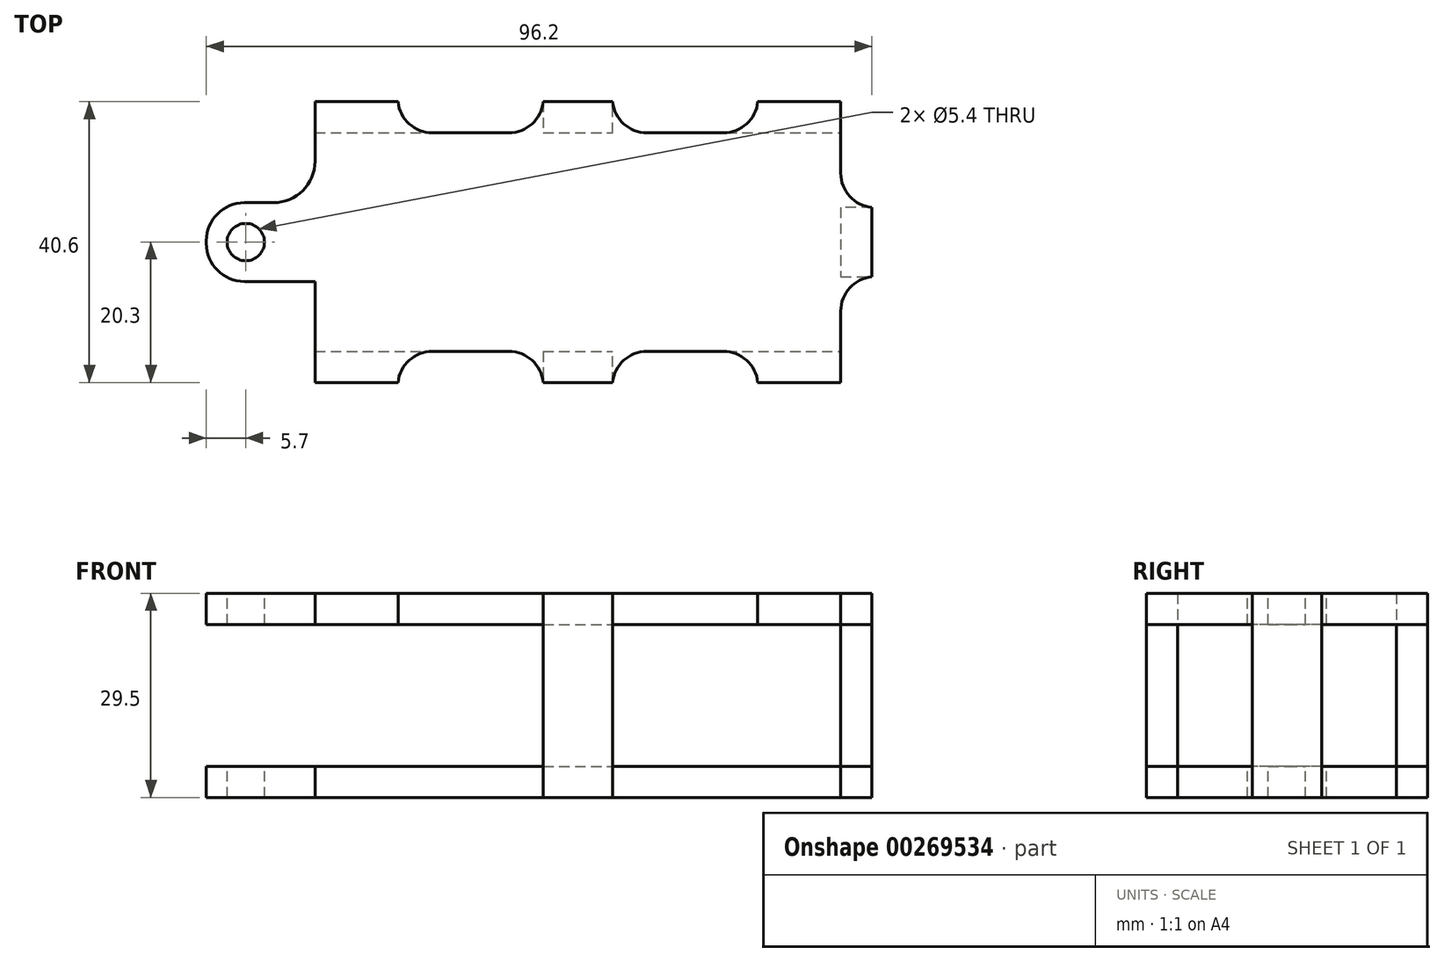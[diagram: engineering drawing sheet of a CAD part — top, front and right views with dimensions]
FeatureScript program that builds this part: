
annotation { "Feature Type Name" : "Feature", "Feature Type Description" : "" }
export const myFeature = defineFeature(function(context is Context, id is Id, definition is map)
    precondition{}
    {
        {
            var Q0;
            Q0=qCreatedBy(makeId("Top.planeOp"),FACE);
            var sketch = newSketch(context, id + "F0", { "sketchPlane" : qUnion([Q0])});
            skLineSegment(sketch, "E0.bottom", {"start": v(0, 31.6) * mm, "end": v(76, 31.6) * mm});
            skLineSegment(sketch, "E0.top", {"start": v(0, 0) * mm, "end": v(76, 0) * mm});
            skLineSegment(sketch, "E0.left", {"start": v(0, 31.6) * mm, "end": v(0, 0) * mm});
            skLineSegment(sketch, "E0.right", {"start": v(76, 31.6) * mm, "end": v(76, 0) * mm});
            skLineSegment(sketch, "E1.bottom", {"start": v(76, 31.6) * mm, "end": v(64, 31.6) * mm});
            skLineSegment(sketch, "E1.top", {"start": v(76, 36.1) * mm, "end": v(64, 36.1) * mm});
            skLineSegment(sketch, "E1.left", {"start": v(76, 31.6) * mm, "end": v(76, 36.1) * mm});
            skLineSegment(sketch, "E1.right", {"start": v(64, 31.6) * mm, "end": v(64, 36.1) * mm});
            skLineSegment(sketch, "E2.bottom", {"start": v(76, 0) * mm, "end": v(64, 0) * mm});
            skLineSegment(sketch, "E2.top", {"start": v(76, -4.5) * mm, "end": v(64, -4.5) * mm});
            skLineSegment(sketch, "E2.left", {"start": v(76, 0) * mm, "end": v(76, -4.5) * mm});
            skLineSegment(sketch, "E2.right", {"start": v(64, 0) * mm, "end": v(64, -4.5) * mm});
            skLineSegment(sketch, "E3.bottom", {"start": v(76, 10.8) * mm, "end": v(80.5, 10.8) * mm});
            skLineSegment(sketch, "E3.top", {"start": v(76, 20.8) * mm, "end": v(80.5, 20.8) * mm});
            skLineSegment(sketch, "E3.left", {"start": v(76, 10.8) * mm, "end": v(76, 20.8) * mm});
            skLineSegment(sketch, "E3.right", {"start": v(80.5, 10.8) * mm, "end": v(80.5, 20.8) * mm});
            skPoint(sketch, "E4", {"position": v(80.5, 15.8) * mm});
            skPoint(sketch, "E5", {"position": v(76, 15.8) * mm});
            skLineSegment(sketch, "E6", {"start": v(80.5, 15.8) * mm, "end": v(76, 15.8) * mm});
            skLineSegment(sketch, "E7.bottom", {"start": v(0, 0) * mm, "end": v(12, 0) * mm});
            skLineSegment(sketch, "E7.top", {"start": v(0, -4.5) * mm, "end": v(12, -4.5) * mm});
            skLineSegment(sketch, "E7.left", {"start": v(0, 0) * mm, "end": v(0, -4.5) * mm});
            skLineSegment(sketch, "E7.right", {"start": v(12, 0) * mm, "end": v(12, -4.5) * mm});
            skLineSegment(sketch, "E8.bottom", {"start": v(0, 31.6) * mm, "end": v(12, 31.6) * mm});
            skLineSegment(sketch, "E8.top", {"start": v(0, 36.1) * mm, "end": v(12, 36.1) * mm});
            skLineSegment(sketch, "E8.left", {"start": v(0, 31.6) * mm, "end": v(0, 36.1) * mm});
            skLineSegment(sketch, "E8.right", {"start": v(12, 31.6) * mm, "end": v(12, 36.1) * mm});
            skPoint(sketch, "E9", {"position": v(38, 0) * mm});
            skPoint(sketch, "E10", {"position": v(38, 31.6) * mm});
            skLineSegment(sketch, "E11.bottom", {"start": v(43, 31.6) * mm, "end": v(33, 31.6) * mm});
            skLineSegment(sketch, "E11.top", {"start": v(43, 36.1) * mm, "end": v(33, 36.1) * mm});
            skLineSegment(sketch, "E11.left", {"start": v(43, 31.6) * mm, "end": v(43, 36.1) * mm});
            skLineSegment(sketch, "E11.right", {"start": v(33, 31.6) * mm, "end": v(33, 36.1) * mm});
            skPoint(sketch, "E11.middle", {"position": v(38, 33.85) * mm});
            skLineSegment(sketch, "E12.bottom", {"start": v(43, 0) * mm, "end": v(33, 0) * mm});
            skLineSegment(sketch, "E12.top", {"start": v(43, -4.5) * mm, "end": v(33, -4.5) * mm});
            skLineSegment(sketch, "E12.left", {"start": v(43, 0) * mm, "end": v(43, -4.5) * mm});
            skLineSegment(sketch, "E12.right", {"start": v(33, 0) * mm, "end": v(33, -4.5) * mm});
            skPoint(sketch, "E12.middle", {"position": v(38, -2.25) * mm});
            skLineSegment(sketch, "E13", {"start": v(38, 33.85) * mm, "end": v(38, 31.6) * mm});
            skLineSegment(sketch, "E14", {"start": v(38, 0) * mm, "end": v(38, -2.25) * mm});
            skSolve(sketch);
        }
        {
            var Q0;
            Q0=makeQuery(id+"F0.imprint","IMPRINT",FACE,{"disambiguationData":[TD([[makeQuery(id+"F0.imprint","IMPRINT",EDGE,{"derivedFrom":sQuery(id+"F0.wireOp",EDGE,"E0.left")}),1.0]])]});
            var Q1;
            Q1=makeQuery(id+"F0.imprint","IMPRINT",FACE,{"disambiguationData":[TD([[makeQuery(id+"F0.imprint","IMPRINT",EDGE,{"derivedFrom":sQuery(id+"F0.wireOp",EDGE,"E7.bottom")}),-1.0]])]});
            var Q2;
            Q2=makeQuery(id+"F0.imprint","IMPRINT",FACE,{"disambiguationData":[TD([[makeQuery(id+"F0.imprint","IMPRINT",EDGE,{"derivedFrom":sQuery(id+"F0.wireOp",EDGE,"E12.top")}),-1.0]])]});
            var Q3;
            Q3=makeQuery(id+"F0.imprint","IMPRINT",FACE,{"disambiguationData":[TD([[makeQuery(id+"F0.imprint","IMPRINT",EDGE,{"derivedFrom":sQuery(id+"F0.wireOp",EDGE,"E2.bottom")}),1.0]])]});
            var Q4;
            {var subQ0=sQuery(id+"F0.wireOp",EDGE,"E3.bottom");Q4=makeQuery(id+"F0.imprint","IMPRINT",FACE,{"disambiguationData":[TD([[makeQuery(id+"F0.imprint","IMPRINT",EDGE,{"derivedFrom":subQ0}),1.0]])]});}
            var Q5;
            {var subQ0=sQuery(id+"F0.wireOp",EDGE,"E3.top");Q5=makeQuery(id+"F0.imprint","IMPRINT",FACE,{"disambiguationData":[TD([[makeQuery(id+"F0.imprint","IMPRINT",EDGE,{"derivedFrom":subQ0}),-1.0]])]});}
            var Q6;
            Q6=makeQuery(id+"F0.imprint","IMPRINT",FACE,{"disambiguationData":[TD([[makeQuery(id+"F0.imprint","IMPRINT",EDGE,{"derivedFrom":sQuery(id+"F0.wireOp",EDGE,"E1.bottom")}),-1.0]])]});
            var Q7;
            Q7=makeQuery(id+"F0.imprint","IMPRINT",FACE,{"disambiguationData":[TD([[makeQuery(id+"F0.imprint","IMPRINT",EDGE,{"derivedFrom":sQuery(id+"F0.wireOp",EDGE,"E11.top")}),1.0]])]});
            var Q8;
            Q8=makeQuery(id+"F0.imprint","IMPRINT",FACE,{"disambiguationData":[TD([[makeQuery(id+"F0.imprint","IMPRINT",EDGE,{"derivedFrom":sQuery(id+"F0.wireOp",EDGE,"E8.bottom")}),1.0]])]});
            extrude(context, id + "F1", {"entities" : qUnion([Q0, Q1, Q2, Q3, Q4, Q5, Q6, Q7, Q8]), "oppositeDirection" : true, "depth" : 4.5 * mm});
        }
        {
            var Q0;
            Q0=makeQuery(id+"F0.imprint","IMPRINT",FACE,{"disambiguationData":[TD([[makeQuery(id+"F0.imprint","IMPRINT",EDGE,{"derivedFrom":sQuery(id+"F0.wireOp",EDGE,"E7.bottom")}),-1.0]])]});
            var Q1;
            Q1=makeQuery(id+"F0.imprint","IMPRINT",FACE,{"disambiguationData":[TD([[makeQuery(id+"F0.imprint","IMPRINT",EDGE,{"derivedFrom":sQuery(id+"F0.wireOp",EDGE,"E12.top")}),-1.0]])]});
            var Q2;
            Q2=makeQuery(id+"F0.imprint","IMPRINT",FACE,{"disambiguationData":[TD([[makeQuery(id+"F0.imprint","IMPRINT",EDGE,{"derivedFrom":sQuery(id+"F0.wireOp",EDGE,"E11.top")}),1.0]])]});
            var Q3;
            Q3=makeQuery(id+"F0.imprint","IMPRINT",FACE,{"disambiguationData":[TD([[makeQuery(id+"F0.imprint","IMPRINT",EDGE,{"derivedFrom":sQuery(id+"F0.wireOp",EDGE,"E8.bottom")}),1.0]])]});
            var Q4;
            Q4=makeQuery(id+"F0.imprint","IMPRINT",FACE,{"disambiguationData":[TD([[makeQuery(id+"F0.imprint","IMPRINT",EDGE,{"derivedFrom":sQuery(id+"F0.wireOp",EDGE,"E2.bottom")}),1.0]])]});
            var Q5;
            {var subQ0=sQuery(id+"F0.wireOp",EDGE,"E3.bottom");Q5=makeQuery(id+"F0.imprint","IMPRINT",FACE,{"disambiguationData":[TD([[makeQuery(id+"F0.imprint","IMPRINT",EDGE,{"derivedFrom":subQ0}),1.0]])]});}
            var Q6;
            {var subQ0=sQuery(id+"F0.wireOp",EDGE,"E3.top");Q6=makeQuery(id+"F0.imprint","IMPRINT",FACE,{"disambiguationData":[TD([[makeQuery(id+"F0.imprint","IMPRINT",EDGE,{"derivedFrom":subQ0}),-1.0]])]});}
            var Q7;
            Q7=makeQuery(id+"F0.imprint","IMPRINT",FACE,{"disambiguationData":[TD([[makeQuery(id+"F0.imprint","IMPRINT",EDGE,{"derivedFrom":sQuery(id+"F0.wireOp",EDGE,"E1.bottom")}),-1.0]])]});
            extrude(context, id + "F2", {"entities" : qUnion([Q0, Q1, Q2, Q3, Q4, Q5, Q6, Q7]), "operationType" : NewBodyOperationType.ADD, "depth" : 20.5 * mm});
        }
        {
            var Q0;
            Q0 = qSketchRegion(id + "F0", true);
            extrude(context, id + "F3", {"entities" : qUnion([Q0]), "operationType" : NewBodyOperationType.ADD, "depth" : 25 * mm, "hasSecondDirection" : true, "secondDirectionOppositeDirection" : false, "secondDirectionDepth" : 20.5 * mm});
        }
        {
            var Q0;
            Q0=makeQuery(id+"F3.opExtrude","SWEPT_EDGE",EDGE,{"disambiguationData":[OSD([sQuery(id+"F0.wireOp",EDGE,"E0.top"),sQuery(id+"F0.wireOp",EDGE,"E7.bottom"),sQuery(id+"F0.wireOp",EDGE,"E7.right")])]});
            var Q1;
            Q1=makeQuery(id+"F1.opExtrude","SWEPT_EDGE",EDGE,{"disambiguationData":[OSD([sQuery(id+"F0.wireOp",EDGE,"E0.top"),sQuery(id+"F0.wireOp",EDGE,"E7.bottom"),sQuery(id+"F0.wireOp",EDGE,"E7.right")])]});
            var Q2;
            Q2=makeQuery(id+"F3.opExtrude","SWEPT_EDGE",EDGE,{"disambiguationData":[OSD([sQuery(id+"F0.wireOp",EDGE,"E0.top"),sQuery(id+"F0.wireOp",EDGE,"E12.bottom"),sQuery(id+"F0.wireOp",EDGE,"E12.right")])]});
            var Q3;
            Q3=makeQuery(id+"F1.opExtrude","SWEPT_EDGE",EDGE,{"disambiguationData":[OSD([sQuery(id+"F0.wireOp",EDGE,"E0.top"),sQuery(id+"F0.wireOp",EDGE,"E12.bottom"),sQuery(id+"F0.wireOp",EDGE,"E12.right")])]});
            var Q4;
            Q4=makeQuery(id+"F3.opExtrude","SWEPT_EDGE",EDGE,{"disambiguationData":[OSD([sQuery(id+"F0.wireOp",EDGE,"E0.top"),sQuery(id+"F0.wireOp",EDGE,"E12.bottom"),sQuery(id+"F0.wireOp",EDGE,"E12.left")])]});
            var Q5;
            Q5=makeQuery(id+"F1.opExtrude","SWEPT_EDGE",EDGE,{"disambiguationData":[OSD([sQuery(id+"F0.wireOp",EDGE,"E0.top"),sQuery(id+"F0.wireOp",EDGE,"E12.bottom"),sQuery(id+"F0.wireOp",EDGE,"E12.left")])]});
            var Q6;
            Q6=makeQuery(id+"F1.opExtrude","SWEPT_EDGE",EDGE,{"disambiguationData":[OSD([sQuery(id+"F0.wireOp",EDGE,"E0.top"),sQuery(id+"F0.wireOp",EDGE,"E2.bottom"),sQuery(id+"F0.wireOp",EDGE,"E2.right")])]});
            var Q7;
            Q7=makeQuery(id+"F3.opExtrude","SWEPT_EDGE",EDGE,{"disambiguationData":[OSD([sQuery(id+"F0.wireOp",EDGE,"E0.top"),sQuery(id+"F0.wireOp",EDGE,"E2.bottom"),sQuery(id+"F0.wireOp",EDGE,"E2.right")])]});
            var Q8;
            Q8=makeQuery(id+"F3.opExtrude","SWEPT_EDGE",EDGE,{"disambiguationData":[OSD([sQuery(id+"F0.wireOp",EDGE,"E0.right"),sQuery(id+"F0.wireOp",EDGE,"E3.bottom"),sQuery(id+"F0.wireOp",EDGE,"E3.left")])]});
            var Q9;
            Q9=makeQuery(id+"F1.opExtrude","SWEPT_EDGE",EDGE,{"disambiguationData":[OSD([sQuery(id+"F0.wireOp",EDGE,"E0.right"),sQuery(id+"F0.wireOp",EDGE,"E3.bottom"),sQuery(id+"F0.wireOp",EDGE,"E3.left")])]});
            var Q10;
            Q10=makeQuery(id+"F3.opExtrude","SWEPT_EDGE",EDGE,{"disambiguationData":[OSD([sQuery(id+"F0.wireOp",EDGE,"E0.right"),sQuery(id+"F0.wireOp",EDGE,"E3.top"),sQuery(id+"F0.wireOp",EDGE,"E3.left")])]});
            var Q11;
            Q11=makeQuery(id+"F1.opExtrude","SWEPT_EDGE",EDGE,{"disambiguationData":[OSD([sQuery(id+"F0.wireOp",EDGE,"E0.right"),sQuery(id+"F0.wireOp",EDGE,"E3.top"),sQuery(id+"F0.wireOp",EDGE,"E3.left")])]});
            var Q12;
            Q12=makeQuery(id+"F3.opExtrude","SWEPT_EDGE",EDGE,{"disambiguationData":[OSD([sQuery(id+"F0.wireOp",EDGE,"E0.bottom"),sQuery(id+"F0.wireOp",EDGE,"E11.bottom"),sQuery(id+"F0.wireOp",EDGE,"E11.left")])]});
            var Q13;
            Q13=makeQuery(id+"F1.opExtrude","SWEPT_EDGE",EDGE,{"disambiguationData":[OSD([sQuery(id+"F0.wireOp",EDGE,"E0.bottom"),sQuery(id+"F0.wireOp",EDGE,"E11.bottom"),sQuery(id+"F0.wireOp",EDGE,"E11.left")])]});
            var Q14;
            Q14=makeQuery(id+"F3.opExtrude","SWEPT_EDGE",EDGE,{"disambiguationData":[OSD([sQuery(id+"F0.wireOp",EDGE,"E0.bottom"),sQuery(id+"F0.wireOp",EDGE,"E8.bottom"),sQuery(id+"F0.wireOp",EDGE,"E8.right")])]});
            var Q15;
            Q15=makeQuery(id+"F1.opExtrude","SWEPT_EDGE",EDGE,{"disambiguationData":[OSD([sQuery(id+"F0.wireOp",EDGE,"E0.bottom"),sQuery(id+"F0.wireOp",EDGE,"E8.bottom"),sQuery(id+"F0.wireOp",EDGE,"E8.right")])]});
            var Q16;
            Q16=makeQuery(id+"F3.opExtrude","SWEPT_EDGE",EDGE,{"disambiguationData":[OSD([sQuery(id+"F0.wireOp",EDGE,"E0.bottom"),sQuery(id+"F0.wireOp",EDGE,"E1.bottom"),sQuery(id+"F0.wireOp",EDGE,"E1.right")])]});
            var Q17;
            Q17=makeQuery(id+"F1.opExtrude","SWEPT_EDGE",EDGE,{"disambiguationData":[OSD([sQuery(id+"F0.wireOp",EDGE,"E0.bottom"),sQuery(id+"F0.wireOp",EDGE,"E1.bottom"),sQuery(id+"F0.wireOp",EDGE,"E1.right")])]});
            fillet(context, id + "F4", {"entities" : qUnion([Q0, Q1, Q2, Q3, Q4, Q5, Q6, Q7, Q8, Q9, Q10, Q11, Q12, Q13, Q14, Q15, Q16, Q17]), "radius" : 5 * mm, "tangentPropagation" : true, "allowEdgeOverflow" : false});
        }
        {
            var Q0;
            Q0=makeQuery(id+"F3.opExtrude","SWEPT_EDGE",EDGE,{"disambiguationData":[OSD([sQuery(id+"F0.wireOp",EDGE,"E0.bottom"),sQuery(id+"F0.wireOp",EDGE,"E11.bottom"),sQuery(id+"F0.wireOp",EDGE,"E11.right")])]});
            var Q1;
            Q1=makeQuery(id+"F1.opExtrude","SWEPT_EDGE",EDGE,{"disambiguationData":[OSD([sQuery(id+"F0.wireOp",EDGE,"E0.bottom"),sQuery(id+"F0.wireOp",EDGE,"E11.bottom"),sQuery(id+"F0.wireOp",EDGE,"E11.right")])]});
            fillet(context, id + "F5", {"entities" : qUnion([Q0, Q1]), "radius" : 5 * mm, "tangentPropagation" : true, "allowEdgeOverflow" : false});
        }
        {
            var Q0;
            Q0=makeQuery(id+"F3.opExtrude","CAP_FACE",FACE,{"disambiguationData":[OSD([sQuery(id+"F0.wireOp",EDGE,"E0.bottom"),sQuery(id+"F0.wireOp",EDGE,"E0.top"),sQuery(id+"F0.wireOp",EDGE,"E0.left"),sQuery(id+"F0.wireOp",EDGE,"E0.right"),sQuery(id+"F0.wireOp",EDGE,"E1.top"),sQuery(id+"F0.wireOp",EDGE,"E1.left"),sQuery(id+"F0.wireOp",EDGE,"E1.right"),sQuery(id+"F0.wireOp",EDGE,"E2.top"),sQuery(id+"F0.wireOp",EDGE,"E2.left"),sQuery(id+"F0.wireOp",EDGE,"E2.right"),sQuery(id+"F0.wireOp",EDGE,"E3.bottom"),sQuery(id+"F0.wireOp",EDGE,"E3.top"),sQuery(id+"F0.wireOp",EDGE,"E3.right"),sQuery(id+"F0.wireOp",EDGE,"E7.top"),sQuery(id+"F0.wireOp",EDGE,"E7.left"),sQuery(id+"F0.wireOp",EDGE,"E7.right"),sQuery(id+"F0.wireOp",EDGE,"E8.top"),sQuery(id+"F0.wireOp",EDGE,"E8.left"),sQuery(id+"F0.wireOp",EDGE,"E8.right"),sQuery(id+"F0.wireOp",EDGE,"E11.top"),sQuery(id+"F0.wireOp",EDGE,"E11.left"),sQuery(id+"F0.wireOp",EDGE,"E11.right"),sQuery(id+"F0.wireOp",EDGE,"E12.top"),sQuery(id+"F0.wireOp",EDGE,"E12.left"),sQuery(id+"F0.wireOp",EDGE,"E12.right")])],"isStart":false});
            var sketch = newSketch(context, id + "F6", { "sketchPlane" : qUnion([Q0])});
            skPoint(sketch, "E15", {"position": v(0, 15.8) * mm});
            skCircle(sketch, "E16", {"center": v(-10, 15.8) * mm, "radius": 2.7 * mm});
            skLineSegment(sketch, "E17.bottom", {"start": v(0, 21.5) * mm, "end": v(-15.7, 21.5) * mm});
            skLineSegment(sketch, "E17.top", {"start": v(0, 10.1) * mm, "end": v(-15.7, 10.1) * mm});
            skLineSegment(sketch, "E17.left", {"start": v(0, 21.5) * mm, "end": v(0, 10.1) * mm});
            skLineSegment(sketch, "E17.right", {"start": v(-15.7, 21.5) * mm, "end": v(-15.7, 10.1) * mm});
            skSolve(sketch);
        }
        {
            var Q0;
            Q0=makeQuery(id+"F6.imprint","IMPRINT",FACE,{"disambiguationData":[TD([[makeQuery(id+"F6.imprint","IMPRINT",EDGE,{"derivedFrom":sQuery(id+"F6.wireOp",EDGE,"E16")}),-1.0]])]});
            extrude(context, id + "F7", {"entities" : qUnion([Q0]), "operationType" : NewBodyOperationType.ADD, "oppositeDirection" : true, "depth" : 29.5 * mm, "hasSecondDirection" : true, "secondDirectionOppositeDirection" : true, "secondDirectionDepth" : 25 * mm});
        }
        {
            var Q0;
            Q0=makeQuery(id+"F6.imprint","IMPRINT",FACE,{"disambiguationData":[TD([[makeQuery(id+"F6.imprint","IMPRINT",EDGE,{"derivedFrom":sQuery(id+"F6.wireOp",EDGE,"E16")}),-1.0]])]});
            extrude(context, id + "F8", {"entities" : qUnion([Q0]), "operationType" : NewBodyOperationType.ADD, "oppositeDirection" : true, "depth" : 4.5 * mm});
        }
        {
            var Q0;
            Q0=makeQuery(id+"F8.opExtrude","SWEPT_EDGE",EDGE,{"disambiguationData":[OSD([sQuery(id+"F0.wireOp",EDGE,"E0.left"),sQuery(id+"F0.wireOp",EDGE,"E7.left"),sQuery(id+"F0.wireOp",EDGE,"E8.left"),sQuery(id+"F6.wireOp",EDGE,"E17.bottom"),sQuery(id+"F6.wireOp",EDGE,"E17.left")])]});
            var Q1;
            Q1=makeQuery(id+"F8.opExtrude","SWEPT_EDGE",EDGE,{"disambiguationData":[OSD([sQuery(id+"F0.wireOp",EDGE,"E0.left"),sQuery(id+"F0.wireOp",EDGE,"E7.left"),sQuery(id+"F0.wireOp",EDGE,"E8.left"),sQuery(id+"F6.wireOp",EDGE,"E17.top"),sQuery(id+"F6.wireOp",EDGE,"E17.left")])]});
            var Q2;
            Q2=makeQuery(id+"F7.opExtrude","SWEPT_EDGE",EDGE,{"disambiguationData":[OSD([sQuery(id+"F0.wireOp",EDGE,"E0.left"),sQuery(id+"F0.wireOp",EDGE,"E7.left"),sQuery(id+"F0.wireOp",EDGE,"E8.left"),sQuery(id+"F6.wireOp",EDGE,"E17.top"),sQuery(id+"F6.wireOp",EDGE,"E17.left")])]});
            var Q3;
            Q3=makeQuery(id+"F7.opExtrude","SWEPT_EDGE",EDGE,{"disambiguationData":[OSD([sQuery(id+"F0.wireOp",EDGE,"E0.left"),sQuery(id+"F0.wireOp",EDGE,"E7.left"),sQuery(id+"F0.wireOp",EDGE,"E8.left"),sQuery(id+"F6.wireOp",EDGE,"E17.bottom"),sQuery(id+"F6.wireOp",EDGE,"E17.left")])]});
            fillet(context, id + "F9", {"entities" : qUnion([Q0, Q1, Q2, Q3]), "radius" : 6 * mm, "tangentPropagation" : true, "allowEdgeOverflow" : false});
        }
        {
            var Q0;
            Q0=makeQuery(id+"F8.opExtrude","SWEPT_EDGE",EDGE,{"disambiguationData":[OSD([sQuery(id+"F6.wireOp",EDGE,"E17.bottom"),sQuery(id+"F6.wireOp",EDGE,"E17.right")])]});
            var Q1;
            Q1=makeQuery(id+"F8.opExtrude","SWEPT_EDGE",EDGE,{"disambiguationData":[OSD([sQuery(id+"F6.wireOp",EDGE,"E17.top"),sQuery(id+"F6.wireOp",EDGE,"E17.right")])]});
            var Q2;
            Q2=makeQuery(id+"F7.opExtrude","SWEPT_EDGE",EDGE,{"disambiguationData":[OSD([sQuery(id+"F6.wireOp",EDGE,"E17.top"),sQuery(id+"F6.wireOp",EDGE,"E17.right")])]});
            var Q3;
            Q3=makeQuery(id+"F7.opExtrude","SWEPT_EDGE",EDGE,{"disambiguationData":[OSD([sQuery(id+"F6.wireOp",EDGE,"E17.bottom"),sQuery(id+"F6.wireOp",EDGE,"E17.right")])]});
            fillet(context, id + "F10", {"entities" : qUnion([Q0, Q1, Q2, Q3]), "radius" : 5.5 * mm, "tangentPropagation" : true, "allowEdgeOverflow" : false});
        }
    });
